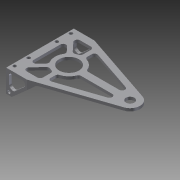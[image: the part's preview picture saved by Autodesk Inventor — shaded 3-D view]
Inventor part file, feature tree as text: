
AUTODESK INVENTOR PART (.ipt)
format: ipt  version: 2012 (Build 160160000, 160)  size: 273,408 bytes
history: native  units: in
note: dims shown in document units (in); Inventor stores cm internally (conversion verified against a paired STEP export)
features: extrude x4, sketch x3, fillet x3, hole x1
ambient origin geometry x8: Origin, YZ Plane, XZ Plane, XY Plane, X Axis, Y Axis, Z Axis, Center Point
bodies: Solid1 (feature_tree)
feature tree (11):
  sketch  "Sketch1"  dims[d0=2.75in d1=4.0in]
  extrude  "Extrusion1"  Depth=4.0in
  extrude  "Extrusion2"  Depth=0.1279in
  fillet  "Fillet1"  Radius=0.375in
  hole  "Hole1"  [1 undecoded]
  sketch  "Sketch2"  dims[d2=1.375in d6=0.1279in d7=0.375in]
  fillet  "Fillet6"  Radius=0.125in
  extrude  "Extrusion7"  Depth=0.625in
  extrude  "Extrusion8"  Depth=0.1562in
  fillet  "Fillet8"  Radius=0.25in
  sketch  "Sketch4"  dims[d8=1.289in d9=0.875in d10=0.125in d11=0.0in d12=0.625in d14=0.1562in d15=0.25in d16=0.25in d17=0.0938in d19=0.0938in d22=0.0938in d24=0.0938in d26=0.1875in d27=0.3125in d28=0.1875in d29=0.125in d30=0.0in d31=0.125in d32=0.125in d33=0.125in d35=0.125in d36=0.125in d38=0.144in d39=0.75in d40=0.25in d41=0.25in d42=0.5635in d43=1.0in d44=0.8108in d51=0.125in d53=0.875in d54=0.0625in d62=0.75in d63=0.75in d69=0.125in d70=0.1279in d71=0.4375in d73=0.125in d75=0.125in d76=0.125in d77=1.0in d78=0.0in d79=0.125in d80=0.125in d81=0.136in d82=0.125in d83=0.25in d84=0.125in d85=0.1875in d86=0.125in d87=0.125in d88=1.0in d89=0.0in d90=0.125in d91=0.1875in d92=0.1875in d93=0.1875in d94=0.1875in d95=0.3125in]
note: 1 required parameter value undecoded (feature->parameter linkage not recoverable at this tier; creation-order binding heuristic only, values carry confidence <= 0.55)
